# Revit family: Overhead_Door-CHI-Planks-LP
name_source: partatom
category: Specialty Equipment
units: mm (PartAtom-declared; Revit-internal decimal feet)

## family parameters
Always vertical = Yes
Cut with Voids When Loaded = No
Host = Wall
OmniClass Number = 23.30.10.21
OmniClass Title = Special Function Doors
Part Type = Normal
Room Calculation Point = No
Round Connector Dimension = Use Diameter
Shared = No

## types (31) — shared parameters
Assembly Code = B2050.10
C Door Bottom Offset = 0.03'
C OFG = 0.00'
C Panel Size = 2
C Side Rail Radius = 1.25'
Certified Windload = Yes
Construction Type = Glass garage doors
Default Elevation = 0.00'
Description = Wood-Look Garage Doors
Fire Rating = Contact Manufacturer for More Information
Glass Finish = Glass - C.H.I Overhead Doors - Frosted
Impact = Yes
Keynote = 08 30 00
Load Classification = Other
Long Panel = Yes
Manufacturer = C.H.I. Overhead Doors
Manufacturer Fax Number = 800-738-5006
Material Disclaimer = Accents Woodtones, when ordered, contain non-repeating patterns. Color discrepancies may appear differently on desktop displays. Contact Manufacturer for Availability of Finishes per Model
Number of Phases = 1
Number of Poles = 1
Product Documentation Link = https://www.chiohd.com
Product Page URL = https://www.chiohd.com
Short Panel = No
Steel Gauge = 27
Thickness = 0.17'
URL = https://www.chiohd.com
Version = 2021-v1.a
Voltage = 115 V

## per-type parameters (varying)
| type | Air Infiltration | C Model | DASMA Thermal Verification Program | Flame Spread | IECC Compliant | Model | Panel Finish | R-Value | U Factor |
| 2347 - Almond | Contact Manufacturer for More Information | 3 | No | Contact Manufacturer for More Information | No | 2347 | Metal - Powder Coat - C.H.I Overhead Doors - Almond | 10.29 | 0.29 |
| 2347 - Black | Contact Manufacturer for More Information | 3 | No | Contact Manufacturer for More Information | No | 2347 | Metal - Powder Coat - C.H.I Overhead Doors - Black | 10.29 | 0.29 |
| 2347 - Bronze | Contact Manufacturer for More Information | 3 | No | Contact Manufacturer for More Information | No | 2347 | Metal - Powder Coat - C.H.I Overhead Doors - Bronze | 10.29 | 0.29 |
| 2347 - Brown | Contact Manufacturer for More Information | 3 | No | Contact Manufacturer for More Information | No | 2347 | Metal - Powder Coat - C.H.I Overhead Doors - Brown | 10.29 | 0.29 |
| 2347 - Graphite | Contact Manufacturer for More Information | 3 | No | Contact Manufacturer for More Information | No | 2347 | Metal - Powder Coat - C.H.I Overhead Doors - Graphite | 10.29 | 0.29 |
| 2347 - Gray | Contact Manufacturer for More Information | 3 | No | Contact Manufacturer for More Information | No | 2347 | Metal - Powder Coat - C.H.I Overhead Doors - Gray | 10.29 | 0.29 |
| 2347 - Sandstone | Contact Manufacturer for More Information | 3 | No | Contact Manufacturer for More Information | No | 2347 | Metal - Powder Coat - C.H.I Overhead Doors - Sandstone | 10.29 | 0.29 |
| 2347 - White | Contact Manufacturer for More Information | 3 | No | Contact Manufacturer for More Information | No | 2347 | Metal - Powder Coat - C.H.I Overhead Doors - White | 10.29 | 0.29 |
| 2347 - Carbon Oak | Contact Manufacturer for More Information | 3 | No | Contact Manufacturer for More Information | No | 2347 | Wood - Accents Woodtones - C.H.I Overhead Doors - Plank - Carbon Oak | 10.29 | 0.29 |
| 2347 - Cedar | Contact Manufacturer for More Information | 3 | No | Contact Manufacturer for More Information | No | 2347 | Wood - Accents Woodtones - C.H.I Overhead Doors - Plank - Cedar | 10.29 | 0.29 |
| 2347 - Dark Oak | Contact Manufacturer for More Information | 3 | No | Contact Manufacturer for More Information | No | 2347 | Wood - Accents Woodtones - C.H.I Overhead Doors - Plank - Dark Oak | 10.29 | 0.29 |
| 2347 - Driftwood | Contact Manufacturer for More Information | 3 | No | Contact Manufacturer for More Information | No | 2347 | Wood - Accents Woodtones - C.H.I Overhead Doors - Plank - Driftwood | 10.29 | 0.29 |
| 2347 - Mahogany | Contact Manufacturer for More Information | 3 | No | Contact Manufacturer for More Information | No | 2347 | Wood - Accents Woodtones - C.H.I Overhead Doors - Plank - Mahogany | 10.29 | 0.29 |
| 2347 - Natural Oak | Contact Manufacturer for More Information | 3 | No | Contact Manufacturer for More Information | No | 2347 | Wood - Accents Woodtones - C.H.I Overhead Doors - Plank - Natural Oak | 10.29 | 0.29 |
| 2347 - Walnut | Contact Manufacturer for More Information | 3 | No | Contact Manufacturer for More Information | No | 2347 | Wood - Accents Woodtones - C.H.I Overhead Doors - Plank - Walnut | 10.29 | 0.29 |
| 2348 - Almond | 0.1 | 4 | Yes | 15 | Yes | 2348 | Metal - Powder Coat - C.H.I Overhead Doors - Almond | 17.54 | 0.19 |
| 2348 - Black | 0.1 | 4 | Yes | 15 | Yes | 2348 | Metal - Powder Coat - C.H.I Overhead Doors - Black | 17.54 | 0.19 |
| 2348 - Bronze | 0.1 | 4 | Yes | 15 | Yes | 2348 | Metal - Powder Coat - C.H.I Overhead Doors - Bronze | 17.54 | 0.19 |
| 2348 - Brown | 0.1 | 4 | Yes | 15 | Yes | 2348 | Metal - Powder Coat - C.H.I Overhead Doors - Brown | 17.54 | 0.19 |
| 2348 - Desert Tan | 0.1 | 4 | Yes | 15 | Yes | 2348 | Metal - Powder Coat - C.H.I Overhead Doors - Desert Tan | 17.54 | 0.19 |
| 2348 - Graphite | 0.1 | 4 | Yes | 15 | Yes | 2348 | Metal - Powder Coat - C.H.I Overhead Doors - Graphite | 17.54 | 0.19 |
| 2348 - Gray | 0.1 | 4 | Yes | 15 | Yes | 2348 | Metal - Powder Coat - C.H.I Overhead Doors - Gray | 17.54 | 0.19 |
| 2348 - Sandstone | 0.1 | 4 | Yes | 15 | Yes | 2348 | Metal - Powder Coat - C.H.I Overhead Doors - Sandstone | 17.54 | 0.19 |
| 2348 - White | 0.1 | 4 | Yes | 15 | Yes | 2348 | Metal - Powder Coat - C.H.I Overhead Doors - White | 17.54 | 0.19 |
| 2348 - Carbon Oak | 0.1 | 4 | Yes | 15 | Yes | 2348 | Wood - Accents Woodtones - C.H.I Overhead Doors - Plank - Carbon Oak | 17.54 | 0.19 |
| 2348 - Cedar | 0.1 | 4 | Yes | 15 | Yes | 2348 | Wood - Accents Woodtones - C.H.I Overhead Doors - Plank - Cedar | 17.54 | 0.19 |
| 2348 - Dark Oak | 0.1 | 4 | Yes | 15 | Yes | 2348 | Wood - Accents Woodtones - C.H.I Overhead Doors - Plank - Dark Oak | 17.54 | 0.19 |
| 2348 - Driftwood | 0.1 | 4 | Yes | 15 | Yes | 2348 | Wood - Accents Woodtones - C.H.I Overhead Doors - Plank - Driftwood | 17.54 | 0.19 |
| 2348 - Mahogany | 0.1 | 4 | Yes | 15 | Yes | 2348 | Wood - Accents Woodtones - C.H.I Overhead Doors - Plank - Mahogany | 17.54 | 0.19 |
| 2348 - Natural Oak | 0.1 | 4 | Yes | 15 | Yes | 2348 | Wood - Accents Woodtones - C.H.I Overhead Doors - Plank - Natural Oak | 17.54 | 0.19 |
| 2348 - Walnut | 0.1 | 4 | Yes | 15 | Yes | 2348 | Wood - Accents Woodtones - C.H.I Overhead Doors - Plank - Walnut | 17.54 | 0.19 |

## geometry (parser evidence)
native form markers: Sweep x39
no freeform markers — native parametric forms only
